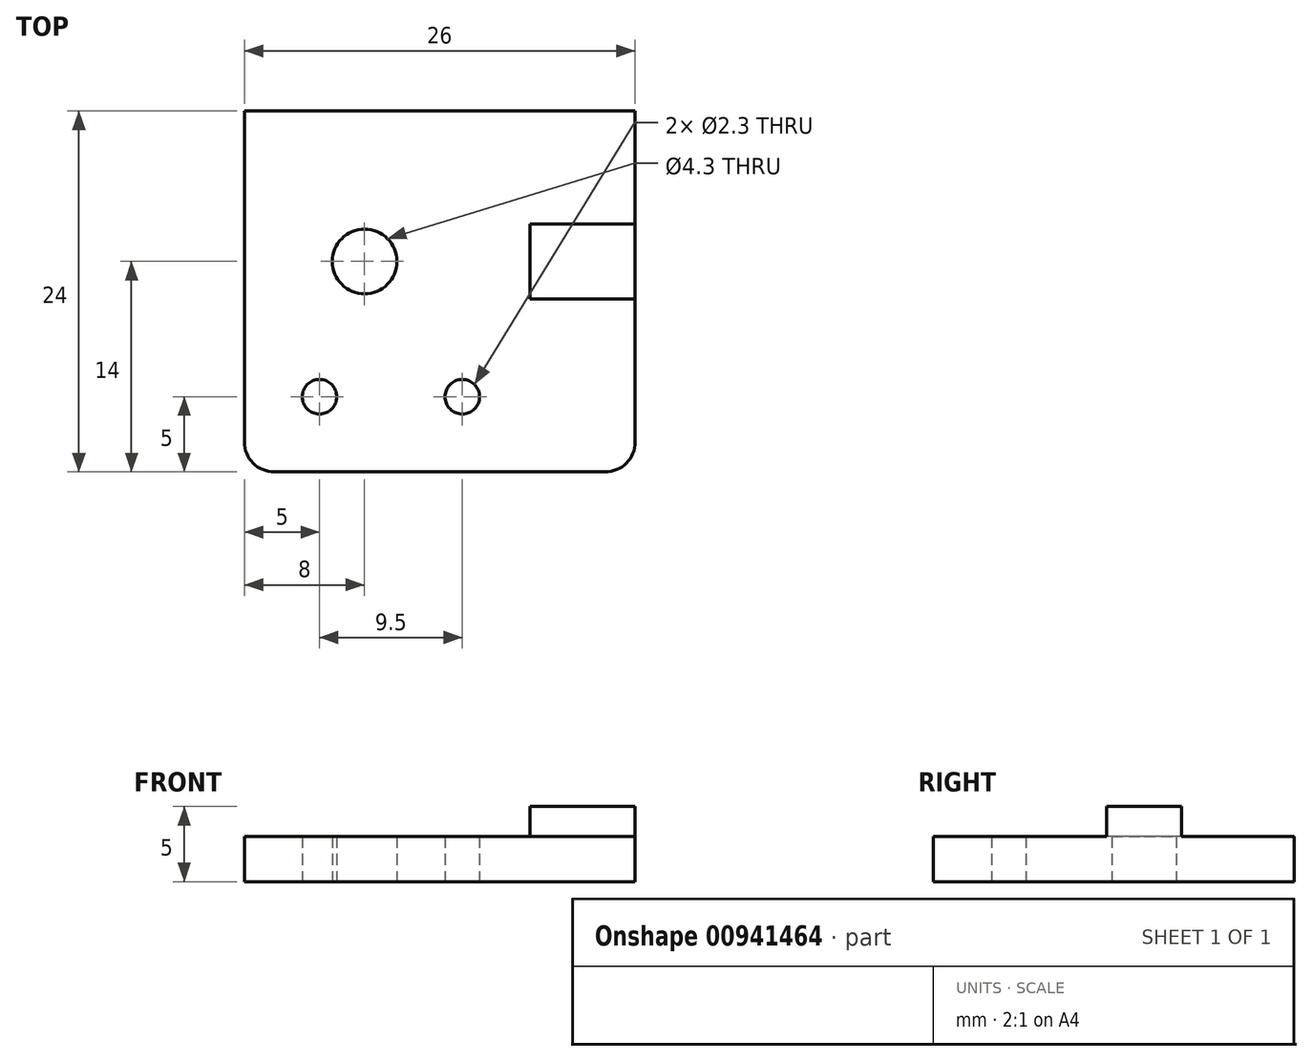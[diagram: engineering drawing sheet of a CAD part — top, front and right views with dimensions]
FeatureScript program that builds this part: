
annotation { "Feature Type Name" : "Feature", "Feature Type Description" : "" }
export const myFeature = defineFeature(function(context is Context, id is Id, definition is map)
    precondition{}
    {
        {
            var Q0;
            Q0=qCreatedBy(makeId("Top.planeOp"),FACE);
            var sketch = newSketch(context, id + "F0", { "sketchPlane" : qUnion([Q0])});
            skLineSegment(sketch, "E0.bottom", {"start": v(0, 0) * mm, "end": v(26, 0) * mm});
            skLineSegment(sketch, "E0.top", {"start": v(0, -24) * mm, "end": v(26, -24) * mm});
            skLineSegment(sketch, "E0.left", {"start": v(0, 0) * mm, "end": v(0, -24) * mm});
            skLineSegment(sketch, "E0.right", {"start": v(26, 0) * mm, "end": v(26, -24) * mm});
            skCircle(sketch, "E1", {"center": v(5, -19) * mm, "radius": 1.15 * mm});
            skCircle(sketch, "E2", {"center": v(14.5, -19) * mm, "radius": 1.15 * mm});
            skCircle(sketch, "E3", {"center": v(8, -10) * mm, "radius": 2.15 * mm});
            skSolve(sketch);
        }
        {
            var Q0;
            Q0=makeQuery(id+"F0.imprint","IMPRINT",FACE,{"disambiguationData":[TD([[makeQuery(id+"F0.imprint","IMPRINT",EDGE,{"derivedFrom":sQuery(id+"F0.wireOp",EDGE,"E0.bottom")}),-1.0]])]});
            extrude(context, id + "F1", {"entities" : qUnion([Q0]), "depth" : 3 * mm, "offsetDistance" : 25 * mm});
        }
        {
            var Q0;
            Q0=makeQuery(id+"F1.opExtrude","CAP_FACE",FACE,{"disambiguationData":[OSD([sQuery(id+"F0.wireOp",EDGE,"E0.bottom"),sQuery(id+"F0.wireOp",EDGE,"E0.top"),sQuery(id+"F0.wireOp",EDGE,"E0.left"),sQuery(id+"F0.wireOp",EDGE,"E0.right"),sQuery(id+"F0.wireOp",EDGE,"E1"),sQuery(id+"F0.wireOp",EDGE,"E2"),sQuery(id+"F0.wireOp",EDGE,"E3")])],"isStart":false});
            var sketch = newSketch(context, id + "F2", { "sketchPlane" : qUnion([Q0])});
            skLineSegment(sketch, "E4.bottom", {"start": v(26, -7.5) * mm, "end": v(19, -7.5) * mm});
            skLineSegment(sketch, "E4.top", {"start": v(26, -12.5) * mm, "end": v(19, -12.5) * mm});
            skLineSegment(sketch, "E4.left", {"start": v(26, -7.5) * mm, "end": v(26, -12.5) * mm});
            skLineSegment(sketch, "E4.right", {"start": v(19, -7.5) * mm, "end": v(19, -12.5) * mm});
            skSolve(sketch);
        }
        {
            var Q0;
            Q0=makeQuery(id+"F2.imprint","IMPRINT",FACE,{"disambiguationData":[TD([[makeQuery(id+"F2.imprint","IMPRINT",EDGE,{"derivedFrom":sQuery(id+"F2.wireOp",EDGE,"E4.bottom")}),1.0]])]});
            extrude(context, id + "F3", {"entities" : qUnion([Q0]), "operationType" : NewBodyOperationType.ADD, "depth" : 2 * mm, "offsetDistance" : 25 * mm});
        }
        {
            var Q0;
            Q0=makeQuery(id+"F1.opExtrude","SWEPT_EDGE",EDGE,{"disambiguationData":[OSD([sQuery(id+"F0.wireOp",EDGE,"E0.top"),sQuery(id+"F0.wireOp",EDGE,"E0.left")])]});
            var Q1;
            Q1=makeQuery(id+"F1.opExtrude","SWEPT_EDGE",EDGE,{"disambiguationData":[OSD([sQuery(id+"F0.wireOp",EDGE,"E0.top"),sQuery(id+"F0.wireOp",EDGE,"E0.right")])]});
            fillet(context, id + "F4", {"entities" : qUnion([Q0, Q1]), "tangentPropagation" : true, "radius" : 2 * mm, "defaultsChanged" : false, "vertexSettings" : [], "allowEdgeOverflow" : false});
        }
    });
